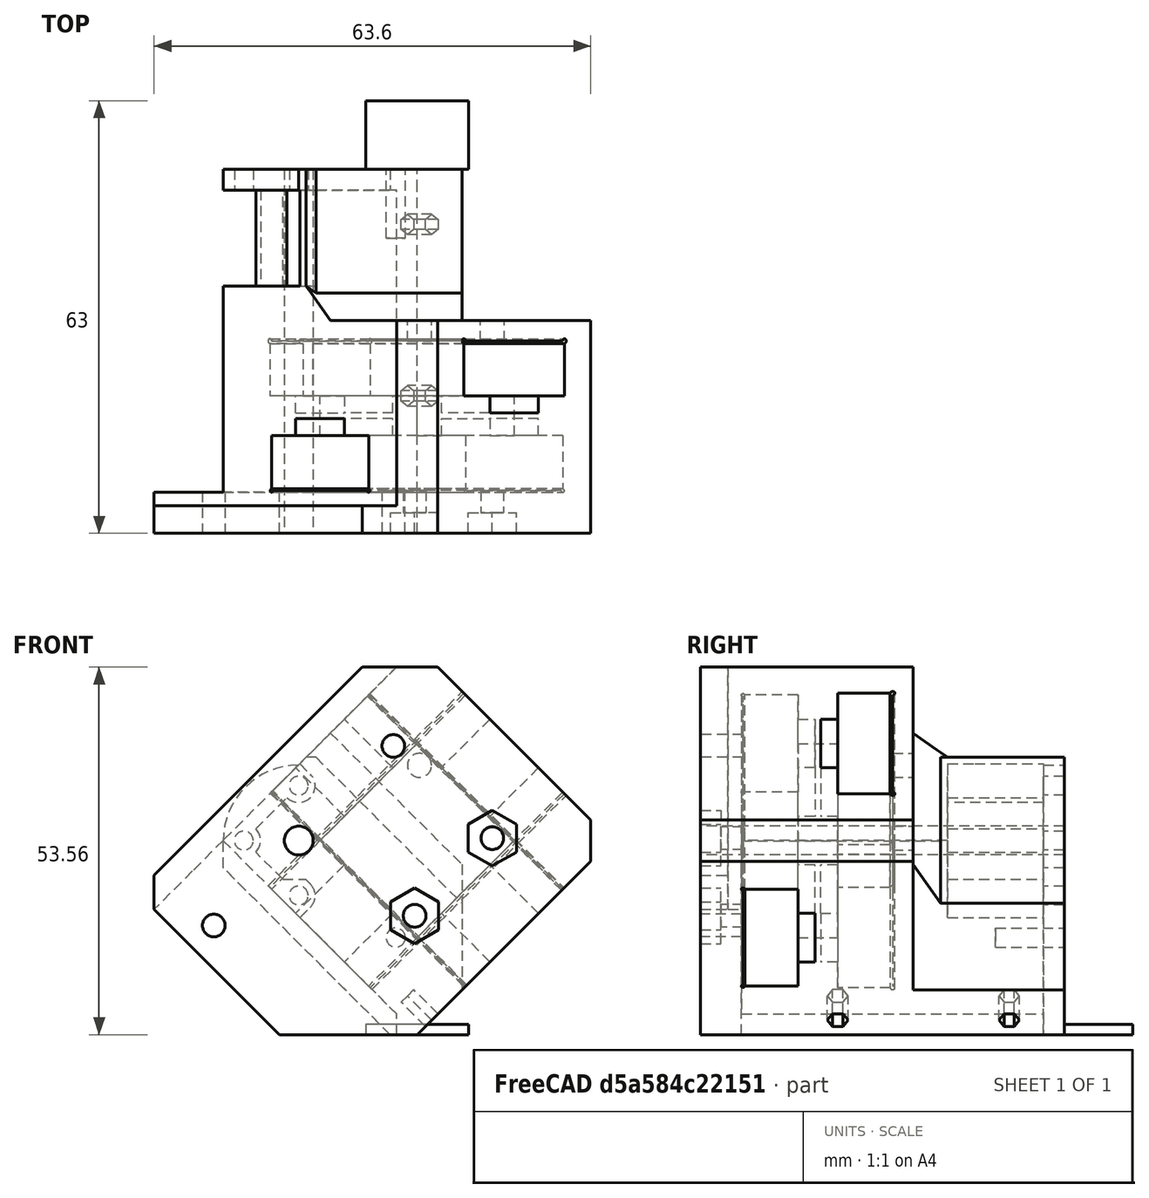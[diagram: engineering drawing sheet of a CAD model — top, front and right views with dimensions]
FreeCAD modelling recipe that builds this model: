
FCSTD DOCUMENT  (FreeCAD 0.19R)
Label: ToolHead_ScreenClearance
License: All rights reserved
LicenseURL: http://en.wikipedia.org/wiki/All_rights_reserved
objects: Sketcher::SketchObject×22, PartDesign::Pocket×14, PartDesign::Pad×5, PartDesign::Chamfer×2, PartDesign::Body×1, Mesh::Feature×1
note: 65 computed .brp shape members not serialized (recipe doc carries the construction recipe); baked Part::Feature solids carry a one-line shape summary decoded from their .brp

FEATURE [Sketcher::SketchObject] Sketch  label="Body001"
  FullyConstrained = true
  MapMode = 5
  Support = -> [XY_Plane]
  sketch-geometry (11):
    g0: LineSegment StartX=20 StartY=15.7574 StartZ=0 EndX=20 EndY=-15.7574 EndZ=0
    g1: LineSegment StartX=15.7574 StartY=-20 StartZ=0 EndX=-20 EndY=-20 EndZ=0
    g2: LineSegment StartX=-20 StartY=-15.7574 StartZ=0 EndX=-20 EndY=19.9515 EndZ=0
    g3: Circle CenterX=-12.1976 CenterY=12.1976 CenterZ=0 NormalX=0 NormalY=0 NormalZ=1 AngleXU=0 Radius=2.1
    g4: LineSegment StartX=-12.1976 StartY=12.1976 StartZ=0 EndX=0 EndY=0 EndZ=0
    g5: ArcOfCircle CenterX=-12.1976 CenterY=12.1976 CenterZ=0 NormalX=0 NormalY=0 NormalZ=1 AngleXU=0 Radius=11 StartAngle=0.788519 EndAngle=2.35931
    g6: LineSegment StartX=-4.44373 StartY=20 StartZ=0 EndX=15.7574 EndY=20 EndZ=0
    g7: LineSegment StartX=15.7574 StartY=-20 StartZ=0 EndX=20 EndY=-15.7574 EndZ=0
    g8: LineSegment StartX=-20 StartY=-15.7574 StartZ=0 EndX=-22.1213 EndY=-17.8787 EndZ=0
    g9: LineSegment StartX=-22.1213 StartY=-17.8787 StartZ=0 EndX=-20 EndY=-20 EndZ=0
    g10: LineSegment StartX=15.7574 StartY=20 StartZ=0 EndX=20 EndY=15.7574 EndZ=0
  constraints (32):
    c: Horizontal(g1)
    c: Vertical(g0)
    c: Vertical(g2)
    c: Distance(g-1,g3) = 17.25
    c: Coincident(g4,g3)
    c: Coincident(g4,g-1)
    c: Angle(g4) = -0.785398
    c: Diameter(g3) = 4.2
    c: Coincident(g5,g3)
    c: Diameter(g5) = 22
    c: DistanceX(g1) = -20
    c: Coincident(g6,g5)
    c: Horizontal(g6)
    c: Coincident(g5,g2)
    c: Coincident(g7,g1)
    c: Coincident(g7,g0)
    c: Angle(g7) = 0.785398
    c: Distance(g7) = 6
    c: DistanceY(g1) = -20
    c: Coincident(g2,g8)
    c: Coincident(g8,g9)
    c: Coincident(g9,g1)
    c: Angle(g9) = -0.785398
    c: Angle(g8) = -2.35619
    c: Distance(g9) = 3
    c: DistanceX(g2) = -20
    c: Coincident(g10,g6)
    c: Coincident(g10,g0)
    c: Distance(g10) = 6
    c: Angle(g10) = -0.785398
    c: DistanceX(g0) = 20
    c: DistanceY(g6) = 20
FEATURE [PartDesign::Pad] Pad
  Direction = (1,1,1)
  Length = 53
  Length2 = 10
  Profile = -> Sketch
  Reversed = true
  Type = 0
FEATURE [Sketcher::SketchObject] Sketch001  label="RailHole"
  FullyConstrained = true
  MapMode = 5
  Placement = pos=(20,0,0) rot=(0.57735,0.57735,0.57735;2.0944rad)
  Support = -> [Pad]
  sketch-geometry (10):
    g0: LineSegment StartX=-10.35 StartY=-27.65 StartZ=0 EndX=-10.35 EndY=-20 EndZ=0
    g1: LineSegment StartX=5 StartY=-17.5 StartZ=0 EndX=-5 EndY=-17.5 EndZ=0
    g2: LineSegment StartX=10 StartY=-28 StartZ=0 EndX=-10 EndY=-28 EndZ=0
    g3: LineSegment StartX=5 StartY=-17.5 StartZ=0 EndX=5 EndY=-20 EndZ=0
    g4: LineSegment StartX=-5 StartY=-20 StartZ=0 EndX=-5 EndY=-17.5 EndZ=0
    g5: LineSegment StartX=-10.35 StartY=-20 StartZ=0 EndX=-5 EndY=-20 EndZ=0
    g6: LineSegment StartX=5 StartY=-20 StartZ=0 EndX=10.3495 EndY=-20 EndZ=0
    g7: LineSegment StartX=10.3495 StartY=-27.65 StartZ=0 EndX=10.3495 EndY=-20 EndZ=0
    g8: ArcOfCircle CenterX=-10.35 CenterY=-28 CenterZ=0 NormalX=0 NormalY=0 NormalZ=1 AngleXU=0 Radius=0.35 StartAngle=1.5708 EndAngle=6.28319
    g9: ArcOfCircle CenterX=10.35 CenterY=-28 CenterZ=0 NormalX=0 NormalY=0 NormalZ=1 AngleXU=0 Radius=0.35 StartAngle=3.14159 EndAngle=7.85541
  constraints (29):
    c: Vertical(g0)
    c: Symmetric(g1,g1,g-2)
    c: Distance(g1) = 10
    c: Coincident(g1,g3)
    c: Vertical(g3)
    c: Coincident(g4,g1)
    c: Symmetric(g3,g4,g-2)
    c: Distance(g3) = 2.5
    c: Distance(g2) = 20
    c: Coincident(g5,g4)
    c: Horizontal(g5)
    c: Coincident(g3,g6)
    c: Horizontal(g6)
    c: Vertical(g7)
    c: Coincident(g0,g5)
    c: Coincident(g7,g6)
    c: Coincident(g0,g8)
    c: Coincident(g8,g2)
    c: Diameter(g8) = 0.7
    c: DistanceX(g0,g8) = 0
    c: DistanceY(g2,g8) = 0
    c: Coincident(g9,g2)
    c: Coincident(g9,g7)
    c: Diameter(g9) = 0.7
    c: DistanceY(g2,g9) = 0
    c: DistanceX(g7,g9) = 0.0005
    c: Symmetric(g9,g8,g-2)
    c: Distance(g9,g6) = 8
    c: DistanceY(g8) = -28
FEATURE [PartDesign::Pocket] Pocket
  BaseFeature = -> Pad
  Length = 5
  Length2 = 100
  Profile = -> Sketch001
  Type = 1
FEATURE [Sketcher::SketchObject] Sketch008  label="ExtruderHole"
  FullyConstrained = false
  MapMode = 5
  Placement = pos=(0,0,4) rot=(0,0,1;0rad)
  sketch-geometry (2):
    g0: LineSegment StartX=0 StartY=0 StartZ=0 EndX=-54.6242 EndY=54.6242 EndZ=0
    g1: Circle CenterX=-12.1976 CenterY=12.1976 CenterZ=0 NormalX=0 NormalY=0 NormalZ=1 AngleXU=0 Radius=2.1
  constraints (5):
    c: Coincident(g0,g-1)
    c: Angle(g0) = 2.35619
    c: PointOnObject(g1,g0)
    c: Distance(g-1,g1) = 17.25
    c: Diameter(g1) = 4.2
FEATURE [Sketcher::SketchObject] Sketch009  label="reference"
  FullyConstrained = false
  MapMode = 5
  Placement = pos=(0,0,-25) rot=(1,0,0;3.14159rad)
  sketch-geometry (2):
    g0: Circle CenterX=-12.0208 CenterY=-12.0208 CenterZ=0 NormalX=0 NormalY=0 NormalZ=1 AngleXU=0 Radius=10
    g1: LineSegment StartX=0 StartY=0 StartZ=0 EndX=-27.7674 EndY=-27.7674 EndZ=0
  constraints (5):
    c: Diameter(g0) = 20
    c: Coincident(g1,g-1)
    c: Angle(g1) = -2.35619
    c: PointOnObject(g0,g1)
    c: Distance(g0,g1) = 17
FEATURE [Sketcher::SketchObject] Sketch010  label="reference2"
  FullyConstrained = false
  MapMode = 5
  Placement = pos=(0,0,-37) rot=(1,0,0;3.14159rad)
  sketch-geometry (2):
    g0: Circle CenterX=-12.1976 CenterY=-12.1976 CenterZ=0 NormalX=0 NormalY=0 NormalZ=1 AngleXU=0 Radius=8
    g1: LineSegment StartX=0 StartY=0 StartZ=0 EndX=-38.1566 EndY=-38.1566 EndZ=0
  constraints (5):
    c: Diameter(g0) = 16
    c: Coincident(g1,g-1)
    c: Angle(g1) = -2.35619
    c: Distance(g0,g1) = 17.25
    c: PointOnObject(g0,g1)
FEATURE [Sketcher::SketchObject] Sketch021  label="InternalTri"
  FullyConstrained = true
  MapMode = 5
  Placement = pos=(0,-3e-15,-12) rot=(0,0,1;0rad)
  sketch-geometry (4):
    g0: LineSegment StartX=-10 StartY=10 StartZ=0 EndX=10 EndY=10 EndZ=0
    g1: LineSegment StartX=10 StartY=10 StartZ=0 EndX=10 EndY=-10 EndZ=0
    g2: LineSegment StartX=10 StartY=-10 StartZ=0 EndX=-10 EndY=-10 EndZ=0
    g3: LineSegment StartX=-10 StartY=-10 StartZ=0 EndX=-10 EndY=10 EndZ=0
  constraints (11):
    c: Coincident(g0,g1)
    c: Coincident(g1,g2)
    c: Coincident(g2,g3)
    c: Coincident(g3,g0)
    c: Horizontal(g0)
    c: Horizontal(g2)
    c: Vertical(g1)
    c: Vertical(g3)
    c: Symmetric(g1,g0,g-1)
    c: Equal(g1,g0)
    c: Distance(g1) = 20
FEATURE [PartDesign::Pocket] Pocket002
  BaseFeature = -> Pocket
  Length = 10
  Length2 = 2
  Profile = -> Sketch021
  Type = 4
FEATURE [Sketcher::SketchObject] Sketch019  label="RailHole2"
  FullyConstrained = true
  MapMode = 5
  Placement = pos=(0,-20,0) rot=(1,0,0;1.5708rad)
  Support = -> [Pocket002]
  sketch-geometry (10):
    g0: LineSegment StartX=-9.75 StartY=-6.2 StartZ=0 EndX=9.75 EndY=-6.2 EndZ=0
    g1: LineSegment StartX=10 StartY=-14.2 StartZ=0 EndX=5 EndY=-14.2 EndZ=0
    g2: LineSegment StartX=5 StartY=-14.2 StartZ=0 EndX=5 EndY=-16.7 EndZ=0
    g3: LineSegment StartX=5 StartY=-16.7 StartZ=0 EndX=-5 EndY=-16.7 EndZ=0
    g4: LineSegment StartX=-5 StartY=-16.7 StartZ=0 EndX=-5 EndY=-14.2 EndZ=0
    g5: LineSegment StartX=-5 StartY=-14.2 StartZ=0 EndX=-10 EndY=-14.2 EndZ=0
    g6: ArcOfCircle CenterX=10 CenterY=-6.2 CenterZ=0 NormalX=0 NormalY=0 NormalZ=1 AngleXU=0 Radius=0.25 StartAngle=4.71239 EndAngle=9.42478
    g7: ArcOfCircle CenterX=-10 CenterY=-6.2 CenterZ=0 NormalX=0 NormalY=0 NormalZ=1 AngleXU=0 Radius=0.25 StartAngle=-9e-16 EndAngle=4.71239
    g8: LineSegment StartX=-10 StartY=-14.2 StartZ=0 EndX=-10 EndY=-6.45 EndZ=0
    g9: LineSegment StartX=10 StartY=-14.2 StartZ=0 EndX=10 EndY=-6.45 EndZ=0
  constraints (29):
    c: Horizontal(g0)
    c: Horizontal(g1)
    c: Coincident(g1,g2)
    c: Vertical(g2)
    c: Coincident(g2,g3)
    c: Horizontal(g3)
    c: Coincident(g3,g4)
    c: Vertical(g4)
    c: Coincident(g4,g5)
    c: Symmetric(g1,g5,g-2)
    c: Distance(g3) = 10
    c: Symmetric(g4,g1,g-2)
    c: DistanceY(g0) = -6.2
    c: Distance(g2) = 2.5
    c: Coincident(g6,g0)
    c: Coincident(g7,g0)
    c: Distance(g7,g6) = 20
    c: DistanceY(g1,g6) = 8
    c: Coincident(g8,g5)
    c: Vertical(g8)
    c: Coincident(g9,g1)
    c: Coincident(g9,g6)
    c: Vertical(g9)
    c: Coincident(g7,g8)
    c: Symmetric(g6,g7,g-2)
    c: Diameter(g6) = 0.5
    c: Equal(g6,g7)
    c: DistanceX(g7,g7) = 0
    c: DistanceY(g7,g0) = 0
FEATURE [Sketcher::SketchObject] Sketch024  label="hgxLITEholes"
  FullyConstrained = false
  MapMode = 5
  Placement = pos=(0,0,4) rot=(0,0,1;0rad)
  sketch-geometry (5):
    g0: Circle CenterX=7.30241 CenterY=12.1976 CenterZ=0 NormalX=0 NormalY=0 NormalZ=1 AngleXU=0 Radius=1.65
    g1: Circle CenterX=-29.6976 CenterY=12.1976 CenterZ=0 NormalX=0 NormalY=0 NormalZ=1 AngleXU=0 Radius=1.65
    g2: LineSegment StartX=-29.6976 StartY=12.1976 StartZ=0 EndX=7.30241 EndY=12.1976 EndZ=0
    g3: LineSegment StartX=0 StartY=0 StartZ=0 EndX=-27.1729 EndY=27.1729 EndZ=0
    g4: Circle CenterX=-12.1976 CenterY=12.1976 CenterZ=0 NormalX=0 NormalY=0 NormalZ=1 AngleXU=0 Radius=1.0154
  constraints (12):
    c: Diameter(g0) = 3.3
    c: Equal(g0,g1)
    c: Coincident(g2,g1)
    c: Coincident(g2,g0)
    c: Distance(g2) = 37
    c: Coincident(g3,g-1)
    c: Angle(g3) = 2.35619
    c: PointOnObject(g4,g3)
    c: Distance(g-1,g4) = 17.25
    c: Distance(g4,g0) = 19.5
    c: Horizontal(g2)
    c: PointOnObject(g4,g2)
FEATURE [PartDesign::Pocket] Pocket003
  BaseFeature = -> Pocket002
  Length = 5
  Length2 = 100
  Profile = -> Sketch019
  Type = 1
FEATURE [Sketcher::SketchObject] Sketch026  label="BottomSculp"
  FullyConstrained = false
  MapMode = 5
  Placement = pos=(0,0,-53) rot=(1,0,0;3.14159rad)
  Support = -> [Pocket003]
  sketch-geometry (5):
    g0: LineSegment StartX=29.4648 StartY=27.8981 StartZ=0 EndX=28.2209 EndY=-23.4245 EndZ=0
    g1: LineSegment StartX=28.2209 StartY=-23.4245 StartZ=0 EndX=-1.84855 EndY=-23.4245 EndZ=0
    g2: LineSegment StartX=-1.84855 StartY=-23.4245 StartZ=0 EndX=-1.84854 EndY=11.0762 EndZ=0
    g3: LineSegment StartX=-1.84854 StartY=11.0762 StartZ=0 EndX=-16.3575 EndY=25.5852 EndZ=0
    g4: LineSegment StartX=-16.3575 StartY=25.5852 StartZ=0 EndX=29.4648 EndY=27.8981 EndZ=0
  constraints (8):
    c: Coincident(g0,g1)
    c: Horizontal(g1)
    c: Coincident(g1,g2)
    c: Angle(g2) = 1.5708
    c: Coincident(g2,g3)
    c: Angle(g3) = 2.35619
    c: Coincident(g4,g3)
    c: Coincident(g4,g0)
FEATURE [PartDesign::Pocket] Pocket004
  BaseFeature = -> Pocket003
  Length = 22
  Length2 = 100
  Profile = -> Sketch026
  Type = 0
FEATURE [Sketcher::SketchObject] Sketch004  label="Yboltpattern"
  FullyConstrained = true
  MapMode = 5
  Placement = pos=(0,0,-31) rot=(1,0,0;3.14159rad)
  Support = -> [Pocket004]
  sketch-geometry (8):
    g0: Circle CenterX=-8 CenterY=7.5 CenterZ=0 NormalX=0 NormalY=0 NormalZ=1 AngleXU=0 Radius=1.75
    g1: Circle CenterX=8 CenterY=7.5 CenterZ=0 NormalX=0 NormalY=0 NormalZ=1 AngleXU=0 Radius=1.75
    g2: Circle CenterX=-8 CenterY=-7.5 CenterZ=0 NormalX=0 NormalY=0 NormalZ=1 AngleXU=0 Radius=1.75
    g3: Circle CenterX=8 CenterY=-7.5 CenterZ=0 NormalX=0 NormalY=0 NormalZ=1 AngleXU=0 Radius=1.75
    g4: LineSegment StartX=-8 StartY=7.5 StartZ=0 EndX=8 EndY=7.5 EndZ=0
    g5: LineSegment StartX=8 StartY=7.5 StartZ=0 EndX=8 EndY=-7.5 EndZ=0
    g6: LineSegment StartX=8 StartY=-7.5 StartZ=0 EndX=-8 EndY=-7.5 EndZ=0
    g7: LineSegment StartX=-8 StartY=-7.5 StartZ=0 EndX=-8 EndY=7.5 EndZ=0
  constraints (18):
    c: Diameter(g0) = 3.5
    c: Equal(g0,g1)
    c: Equal(g0,g2)
    c: Equal(g0,g3)
    c: Distance(g2,g0) = 15
    c: Distance(g3,g2) = 16
    c: Coincident(g4,g0)
    c: Coincident(g4,g1)
    c: Coincident(g4,g5)
    c: Coincident(g5,g3)
    c: Coincident(g5,g6)
    c: Coincident(g6,g2)
    c: Coincident(g6,g7)
    c: Coincident(g7,g4)
    c: Equal(g5,g7)
    c: Equal(g4,g6)
    c: Symmetric(g1,g2,g-1)
    c: Symmetric(g0,g1,g-2)
FEATURE [Sketcher::SketchObject] Sketch022  label="VoronHoleRelif"
  FullyConstrained = true
  MapMode = 5
  Placement = pos=(0,0,-28) rot=(0,0,1;0rad)
  Support = -> [Pocket004]
  sketch-geometry (11):
    g0: ArcOfCircle CenterX=-17.8884 CenterY=6.52425 CenterZ=0 NormalX=0 NormalY=0 NormalZ=1 AngleXU=0 Radius=2.4 StartAngle=4.71239 EndAngle=6.28319
    g1: ArcOfCircle CenterX=-6.58192 CenterY=17.8307 CenterZ=0 NormalX=0 NormalY=0 NormalZ=1 AngleXU=0 Radius=2.4 StartAngle=3.14159 EndAngle=6.28319
    g2: LineSegment StartX=-22.2684 StartY=4.12425 StartZ=0 EndX=-17.8884 EndY=4.12425 EndZ=0
    g3: LineSegment StartX=-22.2684 StartY=23.8307 StartZ=0 EndX=-4.18192 EndY=23.8307 EndZ=0
    g4: LineSegment StartX=-4.18192 StartY=23.8307 StartZ=0 EndX=-4.18192 EndY=17.8307 EndZ=0
    g5: LineSegment StartX=-22.2684 StartY=4.12425 StartZ=0 EndX=-22.2684 EndY=23.8307 EndZ=0
    g6: ArcOfCircle CenterX=-17.8172 CenterY=17.8307 CenterZ=0 NormalX=0 NormalY=0 NormalZ=1 AngleXU=0 Radius=2.4 StartAngle=4.71239 EndAngle=6.28319
    g7: LineSegment StartX=-15.4172 StartY=17.8307 StartZ=0 EndX=-8.98192 EndY=17.8307 EndZ=0
    g8: LineSegment StartX=-17.8172 StartY=9.85307 StartZ=0 EndX=-15.4884 EndY=7.52425 EndZ=0
    g9: LineSegment StartX=-15.4884 StartY=6.52425 StartZ=0 EndX=-15.4884 EndY=7.52425 EndZ=0
    g10: LineSegment StartX=-17.8172 StartY=9.85307 StartZ=0 EndX=-17.8172 EndY=15.4307 EndZ=0
  constraints (33):
    c: Horizontal(g2)
    c: Coincident(g3,g4)
    c: Tangent(g4,g1) = 1.5708
    c: Tangent(g2,g0) = -1.5708
    c: Diameter(g0) = 4.8
    c: Equal(g0,g1)
    c: Vertical(g4)
    c: Horizontal(g3)
    c: Coincident(g5,g2)
    c: Coincident(g5,g3)
    c: Vertical(g5)
    c: Distance(g2) = 4.38
    c: Distance(g4) = 6
    c: DistanceX(g1) = -6.58192
    c: DistanceY(g1) = 17.8307
    c: DistanceX(g0) = -17.8884
    c: DistanceY(g0) = 6.52425
    c: Coincident(g7,g6)
    c: Coincident(g7,g1)
    c: Horizontal(g7)
    c: Perpendicular(g1,g7)
    c: Diameter(g6) = 4.8
    c: Perpendicular(g6,g7)
    c: Angle(g8) = -0.785398
    c: Vertical(g9)
    c: Tangent(g9,g0) = -1.5708
    c: Distance(g9) = 1
    c: Coincident(g8,g9)
    c: Coincident(g10,g8)
    c: Coincident(g10,g6)
    c: Vertical(g10)
    c: Perpendicular(g6,g10)
    c: DistanceX(g6) = -17.8172
FEATURE [PartDesign::Pocket] Pocket005
  BaseFeature = -> Pocket004
  Length = 22
  Length2 = -8
  Profile = -> Sketch022
  Type = 4
FEATURE [Sketcher::SketchObject] Sketch017  label="VoronHoles3"
  FullyConstrained = true
  MapMode = 5
  Placement = pos=(0,0,-50) rot=(0,0,1;0rad)
  Support = -> [Pocket005]
  sketch-geometry (10):
    g0: Circle CenterX=-6.54074 CenterY=17.8544 CenterZ=0 NormalX=0 NormalY=0 NormalZ=1 AngleXU=0 Radius=1.375
    g1: Circle CenterX=-17.8544 CenterY=6.54074 CenterZ=0 NormalX=0 NormalY=0 NormalZ=1 AngleXU=0 Radius=1.375
    g2: Circle CenterX=-6.54074 CenterY=6.54074 CenterZ=0 NormalX=0 NormalY=0 NormalZ=1 AngleXU=0 Radius=1.375
    g3: Circle CenterX=-17.8544 CenterY=17.8544 CenterZ=0 NormalX=0 NormalY=0 NormalZ=1 AngleXU=0 Radius=1.375
    g4: LineSegment StartX=-6.54074 StartY=17.8544 StartZ=0 EndX=-6.54074 EndY=6.54074 EndZ=0
    g5: LineSegment StartX=-6.54074 StartY=6.54074 StartZ=0 EndX=-17.8544 EndY=6.54074 EndZ=0
    g6: LineSegment StartX=-17.8544 StartY=6.54074 StartZ=0 EndX=-17.8544 EndY=17.8544 EndZ=0
    g7: LineSegment StartX=-17.8544 StartY=17.8544 StartZ=0 EndX=-6.54074 EndY=17.8544 EndZ=0
    g8: LineSegment StartX=0 StartY=0 StartZ=0 EndX=-37.1726 EndY=37.1726 EndZ=0
    g9: Circle CenterX=-12.1976 CenterY=12.1976 CenterZ=0 NormalX=0 NormalY=0 NormalZ=1 AngleXU=0 Radius=0.77
  constraints (25):
    c: Coincident(g4,g0)
    c: Coincident(g4,g2)
    c: Coincident(g4,g5)
    c: Coincident(g5,g1)
    c: Coincident(g5,g6)
    c: Coincident(g6,g3)
    c: Coincident(g6,g7)
    c: Coincident(g7,g4)
    c: Equal(g4,g7)
    c: Equal(g7,g6)
    c: Equal(g6,g5)
    c: Coincident(g8,g-1)
    c: PointOnObject(g9,g8)
    c: Distance(g-1,g9) = 17.25
    c: Diameter(g1) = 2.75
    c: Equal(g1,g3)
    c: Equal(g1,g0)
    c: Equal(g1,g2)
    c: Symmetric(g0,g1,g9)
    c: Distance(g2,g3) = 16
    c: Angle(g8) = 2.35619
    c: PointOnObject(g2,g8)
    c: Perpendicular(g7,g4)
    c: Distance(g8) = 52.57
    c: Diameter(g9) = 1.54
FEATURE [PartDesign::Pocket] Pocket006
  BaseFeature = -> Pocket005
  Length = 5
  Length2 = 100
  Profile = -> Sketch017
  Type = 1
FEATURE [Sketcher::SketchObject] Sketch025  label="FanDuctMountHole"
  FullyConstrained = true
  MapMode = 5
  Placement = pos=(0,0,-53) rot=(1,0,0;3.14159rad)
  Support = -> [Pocket006]
  sketch-geometry (1):
    g0: Circle CenterX=-12.2 CenterY=7.8 CenterZ=0 NormalX=0 NormalY=0 NormalZ=1 AngleXU=0 Radius=1.4
  constraints (3):
    c: Diameter(g0) = 2.8
    c: DistanceX(g0) = -12.2
    c: DistanceY(g0) = 7.8
FEATURE [PartDesign::Pocket] Pocket007
  BaseFeature = -> Pocket006
  Length = 10
  Length2 = 100
  Profile = -> Sketch025
  Type = 0
FEATURE [PartDesign::Pocket] Pocket008
  BaseFeature = -> Pocket007
  Length = 9
  Length2 = 100
  Profile = -> Sketch004
  Type = 0
FEATURE [Sketcher::SketchObject] Sketch007  label="ExtruderPlatform"
  ExternalGeometry = -> [Pad]
  FullyConstrained = false
  MapMode = 5
  Support = -> [Pocket008]
  sketch-geometry (12):
    g0: LineSegment StartX=-20 StartY=-20 StartZ=0 EndX=15.7574 EndY=-20 EndZ=0
    g1: LineSegment StartX=0 StartY=0 StartZ=0 EndX=-70.7107 EndY=70.7107 EndZ=0
    g2: Circle CenterX=-12.1976 CenterY=12.1976 CenterZ=0 NormalX=0 NormalY=0 NormalZ=1 AngleXU=0 Radius=2.125
    g3: LineSegment StartX=15.7574 StartY=-20 StartZ=0 EndX=20 EndY=-15.7574 EndZ=0
    g4: LineSegment StartX=20 StartY=-15.7574 StartZ=0 EndX=20 EndY=15.7574 EndZ=0
    g5: LineSegment StartX=20 StartY=15.7574 StartZ=0 EndX=15.7574 EndY=20 EndZ=0
    g6: LineSegment StartX=-20 StartY=-20 StartZ=0 EndX=-34.1976 EndY=-5.80241 EndZ=0
    g7: LineSegment StartX=-12.1976 StartY=-100 StartZ=0 EndX=-12.1976 EndY=100 EndZ=0
    g8: LineSegment StartX=-34.1976 StartY=-5.80241 StartZ=0 EndX=-34.1976 EndY=20 EndZ=0
    g9: LineSegment StartX=-34.1976 StartY=20 StartZ=0 EndX=15.7574 EndY=20 EndZ=0
    g10: Circle CenterX=-29.6976 CenterY=12.1976 CenterZ=0 NormalX=0 NormalY=0 NormalZ=1 AngleXU=0 Radius=1.4
    g11: Circle CenterX=7.30241 CenterY=11.9057 CenterZ=0 NormalX=0 NormalY=0 NormalZ=1 AngleXU=0 Radius=1.4
  constraints (35):
    c: Coincident(g1,g-1)
    c: Angle(g1) = 2.35619
    c: Diameter(g2) = 4.25
    c: PointOnObject(g2,g1)
    c: Distance(g-1,g2) = 17.25
    c: Coincident(g0,g3)
    c: Coincident(g3,g4)
    c: Coincident(g6,g0)
    c: Angle(g6) = 2.35619
    c: Coincident(g5,g4)
    c: Distance(g1) = 100
    c: PointOnObject(g2,g7)
    c: DistanceX(g0,g0) = -35.7574
    c: DistanceY(g0,g0) = 0
    c: DistanceX(g3,g0) = -40
    c: DistanceY(g3,g0) = -4.24264
    c: DistanceX(g4) = 20
    c: DistanceY(g4) = 15.7574
    c: DistanceX(g3) = 20
    c: DistanceY(g3) = -15.7574
    c: Coincident(g8,g6)
    c: Vertical(g8)
    c: Horizontal(g9)
    c: Coincident(g5,g9)
    c: Distance(g8,g7) = 22
    c: DistanceX(g5) = 15.7574
    c: DistanceY(g5) = 20
    c: Symmetric(g7,g7,g-1)
    c: Distance(g7) = 200
    c: DistanceX(g10,g2) = 17.5
    c: DistanceX(g2,g11) = 19.5
    c: Diameter(g10) = 2.8
    c: Equal(g10,g11)
    c: DistanceY(g10,g2) = 0
    c: Coincident(g9,g8)
FEATURE [PartDesign::Pad] Pad001
  BaseFeature = -> Pocket008
  Direction = (1,1,1)
  Length = 6
  Length2 = 100
  Profile = -> Sketch007
  Reversed = true
  Type = 0
FEATURE [PartDesign::Pocket] Pocket009
  BaseFeature = -> Pad001
  Length = 11
  Length2 = 100
  Profile = -> Sketch024
  Type = 0
FEATURE [PartDesign::Pocket] Pocket010
  BaseFeature = -> Pocket009
  Length = 5
  Length2 = 100
  Profile = -> Sketch008
  Type = 1
FEATURE [Sketcher::SketchObject] Sketch003  label="Xboltpattern"
  FullyConstrained = true
  MapMode = 5
  Support = -> [Pocket010]
  sketch-geometry (8):
    g0: Circle CenterX=-8 CenterY=7.5 CenterZ=0 NormalX=0 NormalY=0 NormalZ=1 AngleXU=0 Radius=1.65
    g1: Circle CenterX=8 CenterY=7.5 CenterZ=0 NormalX=0 NormalY=0 NormalZ=1 AngleXU=0 Radius=1.65
    g2: Circle CenterX=-8 CenterY=-7.5 CenterZ=0 NormalX=0 NormalY=0 NormalZ=1 AngleXU=0 Radius=1.65
    g3: Circle CenterX=8 CenterY=-7.5 CenterZ=0 NormalX=0 NormalY=0 NormalZ=1 AngleXU=0 Radius=1.65
    g4: LineSegment StartX=-8 StartY=7.5 StartZ=0 EndX=8 EndY=7.5 EndZ=0
    g5: LineSegment StartX=8 StartY=7.5 StartZ=0 EndX=8 EndY=-7.5 EndZ=0
    g6: LineSegment StartX=8 StartY=-7.5 StartZ=0 EndX=-8 EndY=-7.5 EndZ=0
    g7: LineSegment StartX=-8 StartY=-7.5 StartZ=0 EndX=-8 EndY=7.5 EndZ=0
  constraints (19):
    c: Diameter(g0) = 3.3
    c: Equal(g0,g1)
    c: Equal(g0,g2)
    c: Equal(g0,g3)
    c: Distance(g0,g1) = 16
    c: Distance(g1,g3) = 15
    c: Coincident(g4,g0)
    c: Coincident(g4,g1)
    c: Horizontal(g4)
    c: Coincident(g4,g5)
    c: Coincident(g5,g3)
    c: Vertical(g5)
    c: Coincident(g5,g6)
    c: Coincident(g6,g2)
    c: Coincident(g6,g7)
    c: Coincident(g7,g4)
    c: Symmetric(g2,g1,g-1)
    c: Equal(g7,g5)
    c: Equal(g6,g4)
FEATURE [Sketcher::SketchObject] Sketch029  label="Adhesion"
  FullyConstrained = false
  MapMode = 5
  Placement = pos=(0,0,-53) rot=(1,0,0;3.14159rad)
  sketch-geometry (4):
    g0: LineSegment StartX=-13.636 StartY=24.2426 StartZ=0 EndX=-24.2426 EndY=13.636 EndZ=0
    g1: LineSegment StartX=-24.2426 StartY=13.636 StartZ=0 EndX=-25.3033 EndY=14.6967 EndZ=0
    g2: LineSegment StartX=-25.3033 StartY=14.6967 StartZ=0 EndX=-14.6967 EndY=25.3033 EndZ=0
    g3: LineSegment StartX=-14.6967 StartY=25.3033 StartZ=0 EndX=-13.636 EndY=24.2426 EndZ=0
  constraints (10):
    c: Coincident(g0,g1)
    c: Coincident(g1,g2)
    c: Coincident(g2,g3)
    c: Coincident(g3,g0)
    c: Angle(g2) = 0.785398
    c: Distance(g2) = 15
    c: Distance(g1) = 1.5
    c: Distance(g3) = 1.5
    c: Perpendicular(g2,g3)
    c: Perpendicular(g2,g1)
FEATURE [Sketcher::SketchObject] Sketch033  label="WireMgmnt"
  FullyConstrained = true
  MapMode = 5
  Placement = pos=(0,-20,0) rot=(1,0,0;1.5708rad)
  sketch-geometry (14):
    g0: LineSegment StartX=-15.7 StartY=-20.7506 StartZ=0 EndX=-15.7 EndY=-19.2494 EndZ=0
    g1: LineSegment StartX=-15.7 StartY=-19.2494 StartZ=0 EndX=-17 EndY=-18.4989 EndZ=0
    g2: LineSegment StartX=-17 StartY=-18.4989 StartZ=0 EndX=-18.3 EndY=-19.2494 EndZ=0
    g3: LineSegment StartX=-18.3 StartY=-19.2494 StartZ=0 EndX=-18.3 EndY=-20.7506 EndZ=0
    g4: LineSegment StartX=-18.3 StartY=-20.7506 StartZ=0 EndX=-17 EndY=-21.5011 EndZ=0
    g5: LineSegment StartX=-17 StartY=-21.5011 StartZ=0 EndX=-15.7 EndY=-20.7506 EndZ=0
    g6: Circle CenterX=-17 CenterY=-20 CenterZ=0 NormalX=0 NormalY=0 NormalZ=1 AngleXU=0 Radius=1.50111
    g7: LineSegment StartX=-15.7 StartY=-44.2494 StartZ=0 EndX=-17 EndY=-43.4989 EndZ=0
    g8: LineSegment StartX=-17 StartY=-43.4989 StartZ=0 EndX=-18.3 EndY=-44.2494 EndZ=0
    g9: LineSegment StartX=-18.3 StartY=-44.2494 StartZ=0 EndX=-18.3 EndY=-45.7506 EndZ=0
    g10: LineSegment StartX=-18.3 StartY=-45.7506 StartZ=0 EndX=-17 EndY=-46.5011 EndZ=0
    g11: LineSegment StartX=-17 StartY=-46.5011 StartZ=0 EndX=-15.7 EndY=-45.7506 EndZ=0
    g12: LineSegment StartX=-15.7 StartY=-45.7506 StartZ=0 EndX=-15.7 EndY=-44.2494 EndZ=0
    g13: Circle CenterX=-17 CenterY=-45 CenterZ=0 NormalX=0 NormalY=0 NormalZ=1 AngleXU=0 Radius=1.50111
  constraints (34):
    c: Coincident(g0,g1)
    c: Coincident(g1,g2)
    c: Coincident(g2,g3)
    c: Coincident(g3,g4)
    c: Coincident(g4,g5)
    c: Coincident(g5,g0)
    c: Equal(g0, g1-g5) x5
    c: PointOnObject(g0,g6)
    c: PointOnObject(g1,g6)
    c: PointOnObject(g2,g6)
    c: PointOnObject(g3,g6)
    c: PointOnObject(g4,g6)
    c: PointOnObject(g5,g6)
    c: Coincident(g7,g8)
    c: Coincident(g8,g9)
    c: Coincident(g9,g10)
    c: Coincident(g10,g11)
    c: Coincident(g11,g12)
    c: Coincident(g12,g7)
    c: Equal(g7, g8-g12) x5
    c: PointOnObject(g7,g13)
    c: PointOnObject(g8,g13)
    c: PointOnObject(g9,g13)
    c: PointOnObject(g10,g13)
    c: PointOnObject(g11,g13)
    c: PointOnObject(g12,g13)
    c: DistanceX(g13) = -17
    c: Distance(g10,g7) = 2.6
    c: Vertical(g9)
    c: DistanceY(g13) = -45
    c: Distance(g3,g0) = 2.6
    c: DistanceY(g6) = -20
    c: Vertical(g3)
    c: DistanceX(g6) = -17
FEATURE [Sketcher::SketchObject] Sketch035  label="Bottom Reinforce"
  FullyConstrained = false
  MapMode = 5
  Placement = pos=(0,0,-53) rot=(1,0,0;3.14159rad)
  sketch-geometry (4):
    g0: LineSegment StartX=-22.779 StartY=17.221 StartZ=0 EndX=-22.779 EndY=-17.1725 EndZ=0
    g1: LineSegment StartX=-22.779 StartY=-17.1725 StartZ=0 EndX=-20 EndY=-19.9515 EndZ=0
    g2: LineSegment StartX=-20 StartY=-19.9515 StartZ=0 EndX=-20 EndY=20 EndZ=0
    g3: LineSegment StartX=-20 StartY=20 StartZ=0 EndX=-22.779 EndY=17.221 EndZ=0
  constraints (9):
    c: Vertical(g0)
    c: Coincident(g0,g1)
    c: Coincident(g1,g2)
    c: Vertical(g2)
    c: Coincident(g2,g3)
    c: Coincident(g3,g0)
    c: Angle(g1) = -0.785398
    c: DistanceY(g2) = 20
    c: Angle(g3) = -2.35619
FEATURE [Sketcher::SketchObject] Sketch037
  FullyConstrained = false
  MapMode = 5
  sketch-geometry (4):
    g0: LineSegment StartX=-26.2848 StartY=31.2083 StartZ=0 EndX=-1.26106 EndY=31.2083 EndZ=0
    g1: LineSegment StartX=-1.26106 StartY=31.2083 StartZ=0 EndX=-1.26106 EndY=20 EndZ=0
    g2: LineSegment StartX=-1.26106 StartY=20 StartZ=0 EndX=-26.2848 EndY=20 EndZ=0
    g3: LineSegment StartX=-26.2848 StartY=20 StartZ=0 EndX=-26.2848 EndY=31.2083 EndZ=0
  constraints (9):
    c: Coincident(g0,g1)
    c: Coincident(g1,g2)
    c: Coincident(g2,g3)
    c: Coincident(g3,g0)
    c: Horizontal(g0)
    c: Horizontal(g2)
    c: Vertical(g1)
    c: Vertical(g3)
    c: DistanceY(g1) = 20
FEATURE [PartDesign::Pocket] Pocket011
  BaseFeature = -> Pocket010
  Length = 10
  Length2 = 100
  Profile = -> Sketch003
  Type = 0
FEATURE [Sketcher::SketchObject] Sketch036  label="countersink"
  FullyConstrained = true
  MapMode = 5
  Support = -> [Pocket011]
  sketch-geometry (14):
    g0: LineSegment StartX=11.9037 StartY=-8.546 StartZ=0 EndX=10.8577 EndY=-4.64226 EndZ=0
    g1: LineSegment StartX=10.8577 StartY=-4.64226 StartZ=0 EndX=6.954 EndY=-3.59626 EndZ=0
    g2: LineSegment StartX=6.954 StartY=-3.59626 StartZ=0 EndX=4.09626 EndY=-6.454 EndZ=0
    g3: LineSegment StartX=4.09626 StartY=-6.454 StartZ=0 EndX=5.14226 EndY=-10.3577 EndZ=0
    g4: LineSegment StartX=5.14226 StartY=-10.3577 StartZ=0 EndX=9.046 EndY=-11.4037 EndZ=0
    g5: LineSegment StartX=9.046 StartY=-11.4037 StartZ=0 EndX=11.9037 EndY=-8.546 EndZ=0
    g6: Circle CenterX=8 CenterY=-7.5 CenterZ=0 NormalX=0 NormalY=0 NormalZ=1 AngleXU=0 Radius=4.04145
    g7: LineSegment StartX=-5.14226 StartY=-4.64226 StartZ=0 EndX=-9.046 EndY=-3.59626 EndZ=0
    g8: LineSegment StartX=-9.046 StartY=-3.59626 StartZ=0 EndX=-11.9037 EndY=-6.454 EndZ=0
    g9: LineSegment StartX=-11.9037 StartY=-6.454 StartZ=0 EndX=-10.8577 EndY=-10.3577 EndZ=0
    g10: LineSegment StartX=-10.8577 StartY=-10.3577 StartZ=0 EndX=-6.954 EndY=-11.4037 EndZ=0
    g11: LineSegment StartX=-6.954 StartY=-11.4037 StartZ=0 EndX=-4.09626 EndY=-8.546 EndZ=0
    g12: LineSegment StartX=-4.09626 StartY=-8.546 StartZ=0 EndX=-5.14226 EndY=-4.64226 EndZ=0
    g13: Circle CenterX=-8 CenterY=-7.5 CenterZ=0 NormalX=0 NormalY=0 NormalZ=1 AngleXU=0 Radius=4.04145
  constraints (34):
    c: Coincident(g0,g1)
    c: Coincident(g1,g2)
    c: Coincident(g2,g3)
    c: Coincident(g3,g4)
    c: Coincident(g4,g5)
    c: Coincident(g5,g0)
    c: Equal(g0, g1-g5) x5
    c: PointOnObject(g0,g6)
    c: PointOnObject(g1,g6)
    c: PointOnObject(g2,g6)
    c: PointOnObject(g3,g6)
    c: PointOnObject(g4,g6)
    c: PointOnObject(g5,g6)
    c: Coincident(g7,g8)
    c: Coincident(g8,g9)
    c: Coincident(g9,g10)
    c: Coincident(g10,g11)
    c: Coincident(g11,g12)
    c: Coincident(g12,g7)
    c: Equal(g7, g8-g12) x5
    c: PointOnObject(g7,g13)
    c: PointOnObject(g8,g13)
    c: PointOnObject(g9,g13)
    c: PointOnObject(g10,g13)
    c: PointOnObject(g11,g13)
    c: PointOnObject(g12,g13)
    c: Angle(g11) = 0.785398
    c: Angle(g5) = 0.785398
    c: Distance(g0,g2) = 7
    c: Distance(g7,g8) = 7
    c: DistanceX(g6) = 8
    c: DistanceY(g6) = -7.5
    c: DistanceY(g13) = -7.5
    c: DistanceX(g13) = -8
FEATURE [PartDesign::Pocket] Pocket012
  BaseFeature = -> Pocket011
  Length = 3
  Length2 = 100
  Profile = -> Sketch036
  Type = 0
FEATURE [PartDesign::Pocket] Pocket013
  BaseFeature = -> Pocket012
  Length = 5
  Length2 = 100
  Profile = -> Sketch033
  Type = 0
FEATURE [PartDesign::Pad] Pad002
  BaseFeature = -> Pocket013
  Direction = (1,1,1)
  Length = 3
  Length2 = 100
  Profile = -> Sketch035
  Reversed = true
  Type = 0
FEATURE [PartDesign::Pocket] Pocket014
  BaseFeature = -> Pad002
  Length = 40
  Length2 = 100
  Profile = -> Sketch037
  Type = 0
FEATURE [PartDesign::Pad] Pad003
  BaseFeature = -> Pocket014
  Direction = (1,1,1)
  Length = 10
  Length2 = 100
  Profile = -> Sketch029
  Type = 0
FEATURE [Sketcher::SketchObject] Sketch038
  FullyConstrained = true
  MapMode = 5
  Placement = pos=(0,20,0) rot=(0,0.707107,0.707107;3.14159rad)
  Support = -> [Pad003]
FEATURE [Sketcher::SketchObject] Sketch039
  ExternalGeometry = -> [Pad003]
  FullyConstrained = true
  MapMode = 5
  Support = -> [Pad003]
  sketch-geometry (4):
    g0: LineSegment StartX=-30.6621 StartY=23.5355 StartZ=0 EndX=12.2218 EndY=23.5355 EndZ=0
    g1: LineSegment StartX=12.2218 StartY=23.5355 StartZ=0 EndX=15.7574 EndY=20 EndZ=0
    g2: LineSegment StartX=15.7574 StartY=20 StartZ=0 EndX=-34.1976 EndY=20 EndZ=0
    g3: LineSegment StartX=-34.1976 StartY=20 StartZ=0 EndX=-30.6621 EndY=23.5355 EndZ=0
  constraints (10):
    c: Coincident(g0,g1)
    c: Coincident(g1,g2)
    c: Coincident(g2,g3)
    c: Coincident(g3,g0)
    c: Horizontal(g0)
    c: Distance(g1) = 5
    c: Coincident(g2,g-3)
    c: Coincident(g1,g-4)
    c: Angle(g1) = -0.785398
    c: Angle(g3) = 0.785398
FEATURE [PartDesign::Pad] Pad004
  BaseFeature = -> Pad003
  Direction = (1,1,1)
  Length = 4
  Length2 = 100
  Profile = -> Sketch039
  Reversed = true
  Type = 0
FEATURE [PartDesign::Chamfer] Chamfer
  Angle = 45
  Base = -> Pad004 [Edge142]
  BaseFeature = -> Pad004
  ChamferType = 0
  FlipDirection = false
  Size = 4
  Size2 = 1
  SupportTransform = false
FEATURE [PartDesign::Chamfer] Chamfer001
  Angle = 45
  Base = -> Chamfer [Edge99]
  BaseFeature = -> Chamfer
  ChamferType = 0
  FlipDirection = false
  Size = 1
  Size2 = 1
  SupportTransform = false
FEATURE [PartDesign::Body] Body
  Group = -> [Sketch,Pad,Sketch001,Pocket,Sketch003,Sketch004,Sketch007,Sketch008,Sketch009,Sketch010,Sketch017,Sketch019,Sketch021,Pocket002,Sketch022,Sketch024,Sketch025,Sketch026,Pocket003,Pocket004,Pocket005,Pocket006,Pocket007,Pocket008,Pad001,Pocket009,Pocket010,Sketch029,Sketch033,Sketch035,Sketch036,Sketch037,Pocket011,Pocket012,Pocket013,Pad002,Pocket014,Pad003,Sketch038,Sketch039,Pad004,Chamfer,+1 more]
  Origin = -> Origin
  Placement = pos=(0,0,0) rot=(0.862856,-0.357407,0.357407;1.71777rad)
  Tip = -> Chamfer001
FEATURE [Mesh::Feature] Mesh  label="Chamfer001 (Meshed)"
